# Revit family: Fan_HVLS_RiteHite_Revolution
name_source: partatom
category: Mechanical Equipment
revit_build: Autodesk Revit 2015 (Build: 20140223_1515(x64)
units: mm (PartAtom-declared; Revit-internal decimal feet)

## types (1)
- Fan_HVLS_RiteHite_Revolution
    4 Blade = Yes
    Accent Material = Metal - Aluminum - RiteHite - Polished
    Air Movement (CFM) = As Specified in 23 34 00
    Air Movement (MPH) - Zone 1 = As Specified in 23 34 00
    Air Movement (MPH) - Zone 2 = As Specified in 23 34 00
    Air Movement (MPH) - Zone 3 = As Specified in 23 34 00
    Air Movement (MPH) - Zone 4 = As Specified in 23 34 00
    Assembly Code = D3040100
    Blade Angle = 4.16°
    Blade Length = 9' - 2 9/32"
    Construction Details = http://www.ritehite.com
    Default Elevation = 4' - 0"
    Description = Fan as Specified in 23 34 00
    EA1 = 1
    Expected Lifespan (Years) = 0
    Fan Control = [Variable Speed][Fan Commander][Analog Remote]
    Fan Diameter = 20' - 0"
    Green Building-LEED = http://www.arcat.com
    Installation-Fabrication = http://www.ritehite.com
    Keynote = 23 34 00
    MEP Amperage = 0 A
    MEP Apparent Power = 0 VA
    Maintenance Schedule (Months) = 0
    Manufacturer = Rite-Hite Corp
    Manufacturer Fax = 414-355-9248
    Manufacturer Website = http://www.ritehite.com
    Material = Metal - Aluminum - RiteHite - Polished
    Model = As Specified in 23 34 00
    Motor HP = 2
    Phase = 0
    Product Data = http://www.arcat.com
    Product Properties = http://www.arcat.com
    Revision = R1_11-2010
    Sales Information = http://www.ritehite.com
    Send Message = http://www.arcat.com
    Sound Pressure = 40  to 63 dBA depending on fan speed
    Specification = http://www.arcat.com
    Test Data = http://www.ritehite.com
    Tip Offset = 1' - 0"
    URL = http://www.ritehite.com
    Unit Depth = 20' - 0"
    Unit Width = 20' - 0"
    Voltage_MEP = 0 V
    Warranty Duration (Years) = 0
    Weight = As Specified in 23 34 00
    Zone 1 Radius From Center = 20' - 0"
    Zone 2 Radius From Center = 40' - 0"
    Zone 3 Radius From Center = 60' - 0"
    Zone 4 Radius From Center = 85' - 0"

## geometry (parser evidence)
native form markers: Blend x6, Sweep x7
no freeform markers — native parametric forms only
